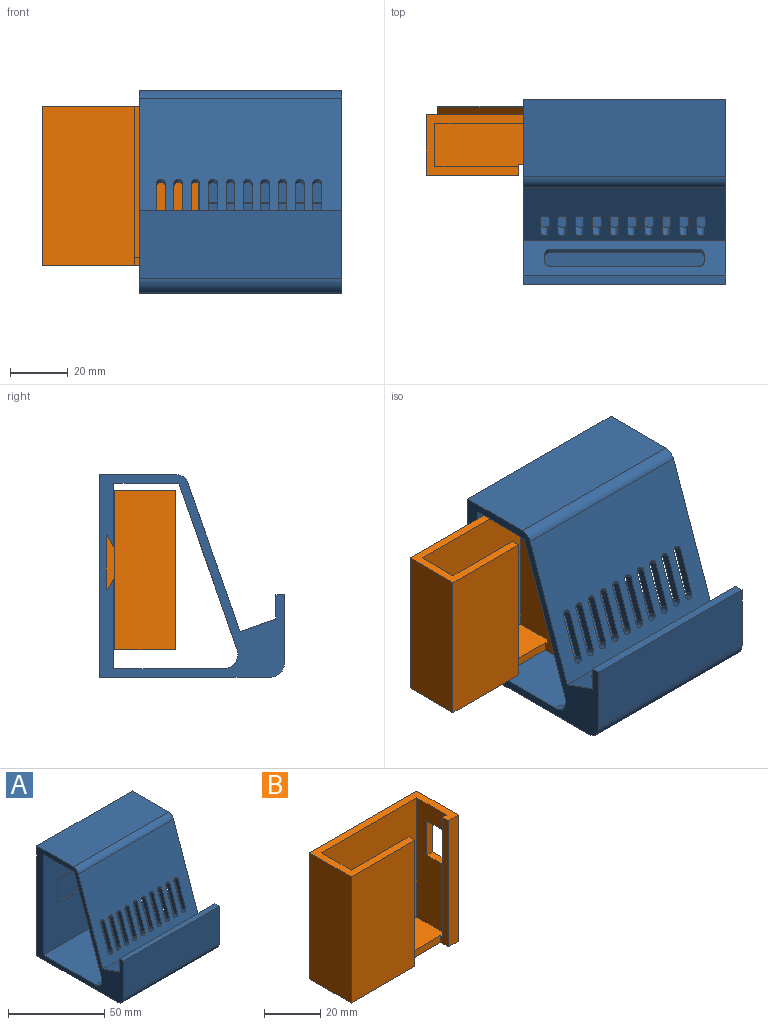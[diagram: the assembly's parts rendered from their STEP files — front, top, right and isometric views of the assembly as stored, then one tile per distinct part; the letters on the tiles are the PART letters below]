
ASSEMBLY  parts=2 mates=2
PART A: 77 faces, bbox 70x64x70 mm
  f0: plane 64x14.24mm, normal (0,-0.33,-0.94), area 637.5mm2, adj f1,f6,f65,f66,f67,f68,f69,f70
  f1: plane 64x11.95mm, normal (0,1,0), area 765mm2, adj f0,f3,f73,f74
  f2: plane 70x54mm, normal (0,0,1), area 3683.1mm2, adj f3,f7,f8,f18,f73,f74,f75,f76
  f3: cylinder r=2mm len=64mm, axis (-1,0,0), area 201.1mm2, adj f1,f2,f73,f74
  f4: plane 70x12.4mm, normal (0,0.33,0.94), area 591.7mm2, adj f5,f8,f15,f18,f65,f66,f67,f68
  f5: plane 70x51.54mm, normal (0,-0.94,0.33), area 3243.2mm2, adj f4,f8,f14,f18,f25,f26,f27,f28
  f6: plane 70x57.34mm, normal (0,0.94,-0.33), area 3517.4mm2, adj f0,f8,f16,f18,f25,f26,f27,f28
  f7: plane 70x64mm, normal (0,-1,0), area 3588mm2, adj f2,f8,f16,f18,f22,f23,f24
  f8: plane 70x64mm, normal (1,0,0), area 991.6mm2, adj f2,f4,f5,f6,f7,f9,f10,f11
  f9: plane 70x23.6mm, normal (0,-1,0), area 1651.6mm2, adj f8,f10,f17,f18
  f10: cylinder r=5mm len=70mm, axis (-1,0,0), area 549.8mm2, adj f8,f9,f11,f18
  f11: plane 70x59mm, normal (0,0,-1), area 4130mm2, adj f8,f10,f12,f18
  f12: plane 70x70mm, normal (0,1,0), area 4900mm2, adj f8,f11,f13,f18
  f13: plane 70x26.74mm, normal (0,0,1), area 1871.6mm2, adj f8,f12,f14,f18
  f14: cylinder r=4mm len=70mm, axis (-1,0,0), area 345.3mm2, adj f5,f8,f13,f18
  f15: plane 70x8.46mm, normal (0,1,0), area 592.4mm2, adj f4,f8,f17,f18
  f16: plane 70x22.45mm, normal (0,0,-1), area 1571.2mm2, adj f6,f7,f8,f18
  f17: plane 70x3mm, normal (0,0,1), area 210mm2, adj f8,f9,f15,f18
  f18: plane 70x64mm, normal (-1,0,0), area 1043.9mm2, adj f2,f4,f5,f6,f7,f9,f10,f11
  f19: plane 60x4.19mm, normal (0,0.87,-0.5), area 290.4mm2, adj f8,f21,f22,f23
  f20: plane 60x4.19mm, normal (0,0.87,0.5), area 290.4mm2, adj f8,f21,f22,f24
  f21: plane 60x23mm, normal (0,-1,0), area 1380mm2, adj f8,f19,f20,f22
  f22: plane 23x2.89mm, normal (1,0,0), area 52.3mm2, adj f7,f19,f20,f21,f23,f24
  f23: cylinder r=0.25mm len=60mm, axis (1,0,0), area 39.3mm2, adj f7,f8,f19,f22
  f24: cylinder r=0.25mm len=60mm, axis (1,0,0), area 39.3mm2, adj f7,f8,f20,f22
  f25: plane 17.03x8.46mm, normal (-1,0,0), area 51mm2, adj f5,f6,f26,f28
  f26: cylinder r=1.5mm len=3.33mm, axis (0,-0.94,0.33), area 14.1mm2, adj f5,f6,f25,f27
  f27: plane 17.03x8.46mm, normal (1,0,0), area 51mm2, adj f5,f6,f26,f28
  f28: cylinder r=1.5mm len=3.33mm, axis (0,-0.94,0.33), area 14.1mm2, adj f5,f6,f25,f27
  f29: plane 17.03x8.46mm, normal (-1,0,0), area 51mm2, adj f5,f6,f30,f32
  f30: cylinder r=1.5mm len=3.33mm, axis (0,-0.94,0.33), area 14.1mm2, adj f5,f6,f29,f31
  f31: plane 17.03x8.46mm, normal (1,0,0), area 51mm2, adj f5,f6,f30,f32
  f32: cylinder r=1.5mm len=3.33mm, axis (0,-0.94,0.33), area 14.1mm2, adj f5,f6,f29,f31
  f33: plane 17.03x8.46mm, normal (-1,0,0), area 51mm2, adj f5,f6,f34,f36
  f34: cylinder r=1.5mm len=3.33mm, axis (0,-0.94,0.33), area 14.1mm2, adj f5,f6,f33,f35
  f35: plane 17.03x8.46mm, normal (1,0,0), area 51mm2, adj f5,f6,f34,f36
  f36: cylinder r=1.5mm len=3.33mm, axis (0,-0.94,0.33), area 14.1mm2, adj f5,f6,f33,f35
  f37: plane 17.03x8.46mm, normal (-1,0,0), area 51mm2, adj f5,f6,f38,f40
  f38: cylinder r=1.5mm len=3.33mm, axis (0,-0.94,0.33), area 14.1mm2, adj f5,f6,f37,f39
  f39: plane 17.03x8.46mm, normal (1,0,0), area 51mm2, adj f5,f6,f38,f40
  f40: cylinder r=1.5mm len=3.33mm, axis (0,-0.94,0.33), area 14.1mm2, adj f5,f6,f37,f39
  f41: plane 17.03x8.46mm, normal (-1,0,0), area 51mm2, adj f5,f6,f42,f44
  f42: cylinder r=1.5mm len=3.33mm, axis (0,-0.94,0.33), area 14.1mm2, adj f5,f6,f41,f43
  f43: plane 17.03x8.46mm, normal (1,0,0), area 51mm2, adj f5,f6,f42,f44
  f44: cylinder r=1.5mm len=3.33mm, axis (0,-0.94,0.33), area 14.1mm2, adj f5,f6,f41,f43
  f45: plane 17.03x8.46mm, normal (-1,0,0), area 51mm2, adj f5,f6,f46,f48
  f46: cylinder r=1.5mm len=3.33mm, axis (0,-0.94,0.33), area 14.1mm2, adj f5,f6,f45,f47
  f47: plane 17.03x8.46mm, normal (1,0,0), area 51mm2, adj f5,f6,f46,f48
  f48: cylinder r=1.5mm len=3.33mm, axis (0,-0.94,0.33), area 14.1mm2, adj f5,f6,f45,f47
  f49: plane 17.03x8.46mm, normal (-1,0,0), area 51mm2, adj f5,f6,f50,f52
  f50: cylinder r=1.5mm len=3.33mm, axis (0,-0.94,0.33), area 14.1mm2, adj f5,f6,f49,f51
  f51: plane 17.03x8.46mm, normal (1,0,0), area 51mm2, adj f5,f6,f50,f52
  f52: cylinder r=1.5mm len=3.33mm, axis (0,-0.94,0.33), area 14.1mm2, adj f5,f6,f49,f51
  f53: plane 17.03x8.46mm, normal (-1,0,0), area 51mm2, adj f5,f6,f54,f56
  f54: cylinder r=1.5mm len=3.33mm, axis (0,-0.94,0.33), area 14.1mm2, adj f5,f6,f53,f55
  f55: plane 17.03x8.46mm, normal (1,0,0), area 51mm2, adj f5,f6,f54,f56
  f56: cylinder r=1.5mm len=3.33mm, axis (0,-0.94,0.33), area 14.1mm2, adj f5,f6,f53,f55
  f57: plane 17.03x8.46mm, normal (-1,0,0), area 51mm2, adj f5,f6,f58,f60
  f58: cylinder r=1.5mm len=3.33mm, axis (0,-0.94,0.33), area 14.1mm2, adj f5,f6,f57,f59
  f59: plane 17.03x8.46mm, normal (1,0,0), area 51mm2, adj f5,f6,f58,f60
  f60: cylinder r=1.5mm len=3.33mm, axis (0,-0.94,0.33), area 14.1mm2, adj f5,f6,f57,f59
  f61: plane 17.03x8.46mm, normal (-1,0,0), area 51mm2, adj f5,f6,f62,f64
  f62: cylinder r=1.5mm len=3.33mm, axis (0,-0.94,0.33), area 14.1mm2, adj f5,f6,f61,f63
  f63: plane 17.03x8.46mm, normal (1,0,0), area 51mm2, adj f5,f6,f62,f64
  f64: cylinder r=1.5mm len=3.33mm, axis (0,-0.94,0.33), area 14.1mm2, adj f5,f6,f61,f63
  f65: plane 3.82x3.82mm, normal (1,0,0), area 9mm2, adj f0,f4,f66,f72
  f66: cylinder r=1.5mm len=3.33mm, axis (0,0.33,0.94), area 7.1mm2, adj f0,f4,f65,f67
  f67: plane 52x2.83mm, normal (0,0.94,-0.33), area 156mm2, adj f0,f4,f66,f68
  f68: cylinder r=1.5mm len=3.33mm, axis (0,0.33,0.94), area 7.1mm2, adj f0,f4,f67,f69
  f69: plane 3.82x3.82mm, normal (-1,0,0), area 9mm2, adj f0,f4,f68,f70
  f70: cylinder r=1.5mm len=3.33mm, axis (0,0.33,0.94), area 7.1mm2, adj f0,f4,f69,f71
  f71: plane 52x2.83mm, normal (0,-0.94,0.33), area 156mm2, adj f0,f4,f70,f72
  f72: cylinder r=1.5mm len=3.33mm, axis (0,0.33,0.94), area 7.1mm2, adj f0,f4,f65,f71
  f73: plane 18.15x13.95mm, normal (-1,0,0), area 159.5mm2, adj f0,f1,f2,f3,f6,f76
  f74: plane 18.15x13.95mm, normal (1,0,0), area 159.5mm2, adj f0,f1,f2,f3,f6,f75
  f75: cylinder r=5mm len=6.66mm, axis (1,0,0), area 28.6mm2, adj f2,f6,f18,f74
  f76: cylinder r=5mm len=6.66mm, axis (-1,0,0), area 28.6mm2, adj f2,f6,f8,f73
PART B: 25 faces, bbox 54x23.9x55 mm
  f0: plane 55x54mm, normal (0,1,0), area 2470mm2, adj f1,f4,f6,f7,f19,f20,f22
  f1: plane 55x23.89mm, normal (1,0,0), area 1048mm2, adj f0,f4,f6,f8,f9,f16,f17,f18
  f2: plane 52x15mm, normal (-1,0,0), area 630mm2, adj f4,f9,f10,f12,f16,f17,f18
  f3: plane 55x32mm, normal (0,-1,0), area 1760mm2, adj f4,f6,f7,f14
  f4: plane 54x21mm, normal (0,0,1), area 363mm2, adj f0,f1,f2,f3,f5,f7,f8,f9
  f5: plane 52x29mm, normal (0,1,0), area 1508mm2, adj f4,f11,f12,f14
  f6: plane 54x21mm, normal (0,0,-1), area 1066mm2, adj f0,f1,f3,f7,f8,f13,f14,f15
  f7: plane 55x21mm, normal (-1,0,0), area 1155mm2, adj f0,f3,f4,f6
  f8: plane 55x5mm, normal (0,-1,0), area 275mm2, adj f1,f4,f6,f13
  f9: plane 52x5mm, normal (0,1,0), area 149mm2, adj f1,f2,f4,f12,f13,f16,f17
  f10: plane 52x48mm, normal (0,-1,0), area 2496mm2, adj f2,f4,f11,f12
  f11: plane 52x15mm, normal (1,0,0), area 780mm2, adj f4,f5,f10,f12
  f12: plane 48x15mm, normal (0,0,1), area 703mm2, adj f2,f5,f9,f10,f11,f13,f14,f15
  f13: plane 55x4mm, normal (-1,0,0), area 168mm2, adj f4,f6,f8,f9,f12,f15
  f14: plane 55x4mm, normal (1,0,0), area 168mm2, adj f3,f4,f5,f6,f12,f15
  f15: plane 17x3mm, normal (0,-1,0), area 51mm2, adj f6,f12,f13,f14
  f16: plane 10x3mm, normal (0,0,-1), area 30mm2, adj f1,f2,f9,f18
  f17: plane 10x3mm, normal (0,0,1), area 30mm2, adj f1,f2,f9,f18
  f18: plane 15x3mm, normal (0,-1,0), area 45mm2, adj f1,f2,f16,f17
  f19: plane 50x4.19mm, normal (0,-0.87,0.5), area 242mm2, adj f0,f1,f22,f24
  f20: plane 50x4.19mm, normal (0,-0.87,-0.5), area 242mm2, adj f0,f1,f22,f23
  f21: plane 50x18.13mm, normal (0,1,0), area 906.7mm2, adj f1,f22,f23,f24
  f22: plane 18.63x2.89mm, normal (-1,0,0), area 43mm2, adj f0,f19,f20,f21,f23,f24
  f23: cylinder r=0.25mm len=50mm, axis (1,0,0), area 32.7mm2, adj f1,f20,f21,f22
  f24: cylinder r=0.25mm len=50mm, axis (1,0,0), area 32.7mm2, adj f1,f19,f21,f22
PLACE A t=(12.07,-12.01,-5.12)mm
PLACE B t=(-29.43,-12.68,-0.11)mm
MATE planar B.f19 <-> A.f19  axis (0,-0.87,0.5) through (-27.43,47.91,41.49)mm
MATE planar B.f21 <-> B.f21  axis (0,1,0) through (-27.43,49.59,34.39)mm
